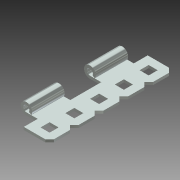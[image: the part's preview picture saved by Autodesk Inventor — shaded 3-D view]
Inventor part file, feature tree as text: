
AUTODESK INVENTOR PART (.ipt)
format: ipt  version: 2013 (Build 170138000, 138)  size: 183,808 bytes
history: native  units: in
note: dims shown in document units (in); Inventor stores cm internally (conversion verified against a paired STEP export)
features: extrude x7, other x5, sketch x3, pattern_linear x1
ambient origin geometry x8: Origin, YZ Plane, XZ Plane, XY Plane, X Axis, Y Axis, Z Axis, Center Point
bodies: Solid1 (feature_tree)
feature tree (16):
  extrude  "Extrusion1"  Depth=0.25in TaperAngle=0.0deg
  extrude  "Extrusion2"  Depth=1.9685in
  pattern_linear  "Rectangular Pattern1"  Spacing1=0.0in  [1 undecoded]
  sketch  "Sketch1"  dims[d0=2.5in d1=0.0in d2=0.25in d3=0.0in]
  sketch  "Sketch2"  dims[d4=0.25in d5=0.0in d6=1.9685in d8=0.5in]
  sketch  "Sketch3"  dims[d9=0.0in d10=0.0in d11=0.0in d12=0.0in d13=0.0in d14=0.0in d15=0.0in d16=0.0in d17=0.0in d18=0.0in]
  other  "Srf1"
  other  "Srf2"
  other  "Srf3"
  other  "Srf4"
  other  "Srf5"
  extrude  "ExtrusionSrf1"  TaperAngle=0.0deg  [1 undecoded]
  extrude  "ExtrusionSrf2"  TaperAngle=0.0deg  [1 undecoded]
  extrude  "ExtrusionSrf3"  TaperAngle=0.0deg  [1 undecoded]
  extrude  "ExtrusionSrf4"  TaperAngle=0.0deg  [1 undecoded]
  extrude  "ExtrusionSrf5"  TaperAngle=0.0deg  [1 undecoded]
note: 6 required parameter values undecoded (feature->parameter linkage not recoverable at this tier; creation-order binding heuristic only, values carry confidence <= 0.55)
